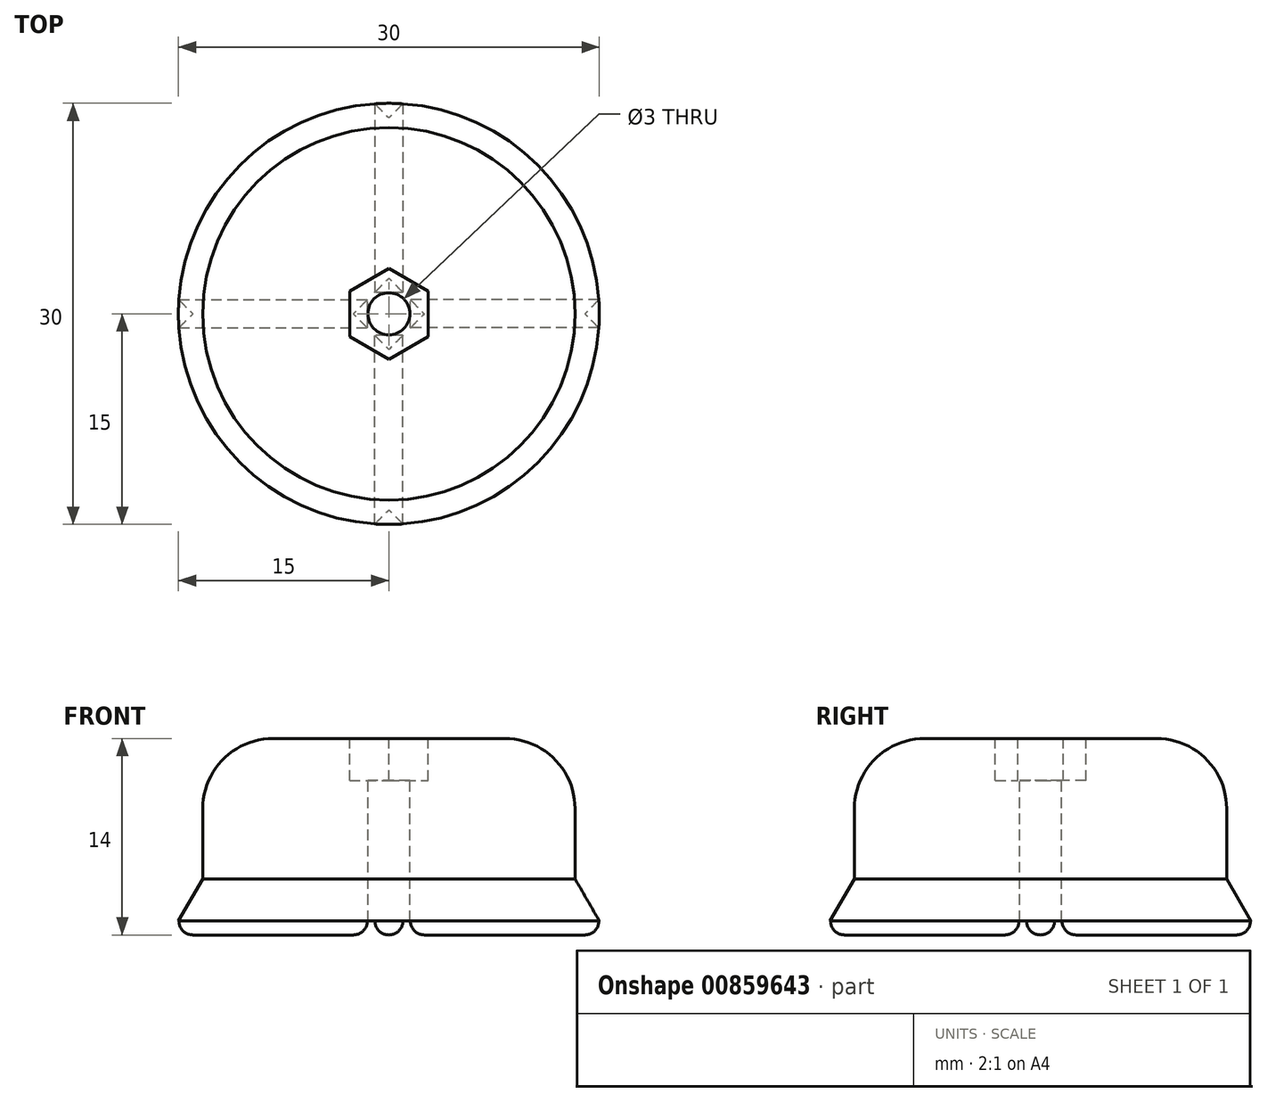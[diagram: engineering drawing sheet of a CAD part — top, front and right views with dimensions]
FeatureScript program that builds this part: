
annotation { "Feature Type Name" : "Feature", "Feature Type Description" : "" }
export const myFeature = defineFeature(function(context is Context, id is Id, definition is map)
    precondition{}
    {
        {
            var Q0;
            Q0=qCreatedBy(makeId("Top.planeOp"),FACE);
            var sketch = newSketch(context, id + "F0", { "sketchPlane" : qUnion([Q0])});
            skCircle(sketch, "E0", {"center": v(0, 0) * mm, "radius": 15 * mm});
            skSolve(sketch);
        }
        {
            var Q0;
            Q0=makeQuery(id+"F0.imprint","IMPRINT",FACE,{"disambiguationData":[TD([[makeQuery(id+"F0.imprint","IMPRINT",EDGE,{"derivedFrom":sQuery(id+"F0.wireOp",EDGE,"E0")}),1.0]])]});
            extrude(context, id + "F1", {"entities" : qUnion([Q0]), "depth" : 3 * mm, "offsetDistance" : 25 * mm, "hasDraft" : true, "draftAngle" : 30 * degree, "draftPullDirection" : true});
        }
        {
            var Q0;
            Q0=makeQuery(id+"F1.opExtrude","CAP_FACE",FACE,{"disambiguationData":[OSD([sQuery(id+"F0.wireOp",EDGE,"E0")])],"isStart":false});
            extrude(context, id + "F2", {"entities" : qUnion([Q0]), "operationType" : NewBodyOperationType.ADD, "depth" : 10 * mm, "offsetDistance" : 25 * mm});
        }
        {
            var Q0;
            Q0=makeQuery(id+"F2.opExtrude","CAP_FACE",FACE,{"disambiguationData":[OSD([sQuery(id+"F0.wireOp",EDGE,"E0")])],"isStart":false});
            var sketch = newSketch(context, id + "F3", { "sketchPlane" : qUnion([Q0])});
            skCircle(sketch, "E1.cCircle", {"center": v(0, 0) * mm, "radius": 2.8 * mm, "construction": true});
            skLineSegment(sketch, "E1.0", {"start": v(2.8, 1.62) * mm, "end": v(2.8, -1.62) * mm});
            skLineSegment(sketch, "E1.1", {"start": v(2.8, -1.62) * mm, "end": v(0, -3.23) * mm});
            skLineSegment(sketch, "E1.2", {"start": v(0, -3.23) * mm, "end": v(-2.8, -1.62) * mm});
            skLineSegment(sketch, "E1.3", {"start": v(-2.8, -1.62) * mm, "end": v(-2.8, 1.62) * mm});
            skLineSegment(sketch, "E1.4", {"start": v(-2.8, 1.62) * mm, "end": v(0, 3.23) * mm});
            skLineSegment(sketch, "E1.5", {"start": v(0, 3.23) * mm, "end": v(2.8, 1.62) * mm});
            skPoint(sketch, "E1.0.midPoint", {"position": v(2.8, 0) * mm});
            skSolve(sketch);
        }
        {
            var Q0;
            Q0=makeQuery(id+"F3.imprint","IMPRINT",FACE,{"disambiguationData":[TD([[makeQuery(id+"F3.imprint","IMPRINT",EDGE,{"derivedFrom":sQuery(id+"F3.wireOp",EDGE,"E1.0")}),-1.0]])]});
            extrude(context, id + "F4", {"entities" : qUnion([Q0]), "operationType" : NewBodyOperationType.REMOVE, "oppositeDirection" : true, "depth" : 3 * mm, "offsetDistance" : 25 * mm});
        }
        {
            var Q0;
            Q0=makeQuery(id+"F4.boolean.opBoolean","COPY",FACE,{"derivedFrom":makeQuery(id+"F4.opExtrude","CAP_FACE",FACE,{"disambiguationData":[OSD([sQuery(id+"F3.wireOp",EDGE,"E1.0"),sQuery(id+"F3.wireOp",EDGE,"E1.1"),sQuery(id+"F3.wireOp",EDGE,"E1.2"),sQuery(id+"F3.wireOp",EDGE,"E1.3"),sQuery(id+"F3.wireOp",EDGE,"E1.4"),sQuery(id+"F3.wireOp",EDGE,"E1.5")])],"isStart":false})});
            var sketch = newSketch(context, id + "F5", { "sketchPlane" : qUnion([Q0])});
            skCircle(sketch, "E2", {"center": v(0, 0) * mm, "radius": 1.5 * mm});
            skSolve(sketch);
        }
        {
            var Q0;
            Q0=makeQuery(id+"F5.imprint","IMPRINT",FACE,{"disambiguationData":[TD([[makeQuery(id+"F5.imprint","IMPRINT",EDGE,{"derivedFrom":sQuery(id+"F5.wireOp",EDGE,"E2")}),1.0]])]});
            extrude(context, id + "F6", {"entities" : qUnion([Q0]), "operationType" : NewBodyOperationType.REMOVE, "endBound" : BoundingType.THROUGH_ALL, "oppositeDirection" : true, "depth" : 25 * mm, "offsetDistance" : 25 * mm});
        }
        {
            var Q0;
            Q0=makeQuery(id+"F1.opExtrude","CAP_FACE",FACE,{"disambiguationData":[OSD([sQuery(id+"F0.wireOp",EDGE,"E0")])],"isStart":true});
            var sketch = newSketch(context, id + "F7", { "sketchPlane" : qUnion([Q0])});
            skLineSegment(sketch, "E3", {"start": v(-1.5, 0) * mm, "end": v(-15, 0) * mm, "construction": true});
            skLineSegment(sketch, "E4", {"start": v(0, 1.5) * mm, "end": v(0, 15) * mm, "construction": true});
            skLineSegment(sketch, "E5", {"start": v(1.5, 0) * mm, "end": v(15, 0) * mm, "construction": true});
            skLineSegment(sketch, "E6", {"start": v(0, -15) * mm, "end": v(0, -1.5) * mm, "construction": true});
            skLineSegment(sketch, "E7.bottom", {"start": v(1, 14.97) * mm, "end": v(-1, 14.97) * mm});
            skLineSegment(sketch, "E7.top", {"start": v(1, 1.53) * mm, "end": v(-1, 1.53) * mm});
            skLineSegment(sketch, "E7.left", {"start": v(1, 14.97) * mm, "end": v(1, 1.53) * mm});
            skLineSegment(sketch, "E7.right", {"start": v(-1, 14.97) * mm, "end": v(-1, 1.53) * mm});
            skPoint(sketch, "E7.middle", {"position": v(0, 8.25) * mm});
            skLineSegment(sketch, "E8.bottom", {"start": v(14.97, 1) * mm, "end": v(1.53, 1) * mm});
            skLineSegment(sketch, "E8.top", {"start": v(14.97, -1) * mm, "end": v(1.53, -1) * mm});
            skLineSegment(sketch, "E8.left", {"start": v(14.97, 1) * mm, "end": v(14.97, -1) * mm});
            skLineSegment(sketch, "E8.right", {"start": v(1.53, 1) * mm, "end": v(1.53, -1) * mm});
            skPoint(sketch, "E8.middle", {"position": v(8.25, 0) * mm});
            skLineSegment(sketch, "E9.MirrorCS", {"start": v(0, 17) * mm, "end": v(0, 3.5) * mm, "construction": true});
            skLineSegment(sketch, "E10.MirrorCS", {"start": v(-14.97, 1) * mm, "end": v(-1.53, 1) * mm});
            skLineSegment(sketch, "E11.MirrorCS", {"start": v(-14.97, -1) * mm, "end": v(-1.53, -1) * mm});
            skLineSegment(sketch, "E12.MirrorCS", {"start": v(-1.53, 1) * mm, "end": v(-1.53, -1) * mm});
            skLineSegment(sketch, "E13.MirrorCS", {"start": v(-14.97, 1) * mm, "end": v(-14.97, -1) * mm});
            skLineSegment(sketch, "E14.MirrorCS", {"start": v(1, -14.97) * mm, "end": v(1, -1.53) * mm});
            skLineSegment(sketch, "E15.MirrorCS", {"start": v(1, -1.53) * mm, "end": v(-1, -1.53) * mm});
            skLineSegment(sketch, "E16.MirrorCS", {"start": v(-1, -14.97) * mm, "end": v(-1, -1.53) * mm});
            skLineSegment(sketch, "E17.MirrorCS", {"start": v(1, -14.97) * mm, "end": v(-1, -14.97) * mm});
            skSolve(sketch);
        }
        {
            var Q0;
            Q0=makeQuery(id+"F7.imprint","IMPRINT",FACE,{"disambiguationData":[TD([[makeQuery(id+"F7.imprint","IMPRINT",EDGE,{"derivedFrom":sQuery(id+"F7.wireOp",EDGE,"E10.MirrorCS")}),-1.0]])]});
            var Q1;
            Q1=makeQuery(id+"F7.imprint","IMPRINT",FACE,{"disambiguationData":[TD([[makeQuery(id+"F7.imprint","IMPRINT",EDGE,{"derivedFrom":sQuery(id+"F7.wireOp",EDGE,"E7.bottom")}),1.0]])]});
            var Q2;
            Q2=makeQuery(id+"F7.imprint","IMPRINT",FACE,{"disambiguationData":[TD([[makeQuery(id+"F7.imprint","IMPRINT",EDGE,{"derivedFrom":sQuery(id+"F7.wireOp",EDGE,"E8.bottom")}),1.0]])]});
            var Q3;
            Q3=makeQuery(id+"F7.imprint","IMPRINT",FACE,{"disambiguationData":[TD([[makeQuery(id+"F7.imprint","IMPRINT",EDGE,{"derivedFrom":sQuery(id+"F7.wireOp",EDGE,"E14.MirrorCS")}),1.0]])]});
            extrude(context, id + "F8", {"entities" : qUnion([Q0, Q1, Q2, Q3]), "operationType" : NewBodyOperationType.ADD, "depth" : 1 * mm, "offsetDistance" : 25 * mm});
        }
        {
            var Q0;
            Q0=makeQuery(id+"F8.opExtrude","CAP_EDGE",EDGE,{"disambiguationData":[OSD([sQuery(id+"F7.wireOp",EDGE,"E16.MirrorCS")])],"isStart":false});
            var Q1;
            Q1=makeQuery(id+"F8.opExtrude","CAP_EDGE",EDGE,{"disambiguationData":[OSD([sQuery(id+"F7.wireOp",EDGE,"E14.MirrorCS")])],"isStart":false});
            var Q2;
            Q2=makeQuery(id+"F8.opExtrude","CAP_EDGE",EDGE,{"disambiguationData":[OSD([sQuery(id+"F7.wireOp",EDGE,"E8.top")])],"isStart":false});
            var Q3;
            Q3=makeQuery(id+"F8.opExtrude","CAP_FACE",FACE,{"disambiguationData":[OSD([sQuery(id+"F7.wireOp",EDGE,"E8.bottom"),sQuery(id+"F7.wireOp",EDGE,"E8.top"),sQuery(id+"F7.wireOp",EDGE,"E8.left"),sQuery(id+"F7.wireOp",EDGE,"E8.right")])],"isStart":false});
            var Q4;
            Q4=makeQuery(id+"F8.opExtrude","CAP_EDGE",EDGE,{"disambiguationData":[OSD([sQuery(id+"F7.wireOp",EDGE,"E11.MirrorCS")])],"isStart":false});
            var Q5;
            Q5=makeQuery(id+"F8.opExtrude","CAP_EDGE",EDGE,{"disambiguationData":[OSD([sQuery(id+"F7.wireOp",EDGE,"E10.MirrorCS")])],"isStart":false});
            var Q6;
            Q6=makeQuery(id+"F8.opExtrude","CAP_EDGE",EDGE,{"disambiguationData":[OSD([sQuery(id+"F7.wireOp",EDGE,"E7.left")])],"isStart":false});
            var Q7;
            Q7=makeQuery(id+"F8.opExtrude","CAP_EDGE",EDGE,{"disambiguationData":[OSD([sQuery(id+"F7.wireOp",EDGE,"E7.right")])],"isStart":false});
            var Q8;
            Q8=makeQuery(id+"F8.opExtrude","CAP_EDGE",EDGE,{"disambiguationData":[OSD([sQuery(id+"F7.wireOp",EDGE,"E17.MirrorCS")])],"isStart":false});
            var Q9;
            Q9=makeQuery(id+"F8.opExtrude","CAP_EDGE",EDGE,{"disambiguationData":[OSD([sQuery(id+"F7.wireOp",EDGE,"E15.MirrorCS")])],"isStart":false});
            var Q10;
            Q10=makeQuery(id+"F8.opExtrude","CAP_EDGE",EDGE,{"disambiguationData":[OSD([sQuery(id+"F7.wireOp",EDGE,"E7.top")])],"isStart":false});
            var Q11;
            Q11=makeQuery(id+"F8.opExtrude","CAP_EDGE",EDGE,{"disambiguationData":[OSD([sQuery(id+"F7.wireOp",EDGE,"E12.MirrorCS")])],"isStart":false});
            var Q12;
            Q12=makeQuery(id+"F8.opExtrude","CAP_EDGE",EDGE,{"disambiguationData":[OSD([sQuery(id+"F7.wireOp",EDGE,"E13.MirrorCS")])],"isStart":false});
            var Q13;
            Q13=makeQuery(id+"F8.opExtrude","CAP_EDGE",EDGE,{"disambiguationData":[OSD([sQuery(id+"F7.wireOp",EDGE,"E7.bottom")])],"isStart":false});
            fillet(context, id + "F9", {"entities" : qUnion([Q0, Q1, Q2, Q3, Q4, Q5, Q6, Q7, Q8, Q9, Q10, Q11, Q12, Q13]), "radius" : 1 * mm, "tangentPropagation" : true, "allowEdgeOverflow" : false});
        }
        {
            var Q0;
            Q0=makeQuery(id+"F2.opExtrude","CAP_EDGE",EDGE,{"disambiguationData":[OSD([sQuery(id+"F0.wireOp",EDGE,"E0")])],"isStart":false});
            fillet(context, id + "F10", {"entities" : qUnion([Q0]), "radius" : 5 * mm, "tangentPropagation" : true, "allowEdgeOverflow" : false});
        }
    });
